annotation { "Feature Type Name" : "Feature", "Feature Type Description" : "" }
export const myFeature = defineFeature(function(context is Context, id is Id, definition is map)
    precondition{}
    {
        {
            var Q0;
            Q0=qCreatedBy(makeId("Front.planeOp"),FACE);
            var sketch = newSketch(context, id + "F0", { "sketchPlane" : qUnion([Q0])});
            skLineSegment(sketch, "E0.1", {"start": v(-0.04, 26) * mm, "end": v(22.5, 13.04) * mm});
            skLineSegment(sketch, "E0.2", {"start": v(22.5, 13.04) * mm, "end": v(22.54, -12.96) * mm});
            skLineSegment(sketch, "E0.3", {"start": v(22.54, -12.96) * mm, "end": v(15.83, -16.85) * mm});
            skLineSegment(sketch, "E0.4", {"start": v(-6.46, -22.26) * mm, "end": v(-7.97, -21.4) * mm});
            skPoint(sketch, "E0.0.midPoint", {"position": v(-11.3, 19.48) * mm});
            skLineSegment(sketch, "E1", {"start": v(-0.04, 26) * mm, "end": v(0.04, -26) * mm});
            skLineSegment(sketch, "E2.0", {"start": v(7.98, 13.23) * mm, "end": v(8.04, -21.37) * mm});
            skLineSegment(sketch, "E3.0", {"start": v(15.78, 9.24) * mm, "end": v(15.83, -16.85) * mm});
            skLineSegment(sketch, "E4", {"start": v(6.48, 14) * mm, "end": v(7.98, 13.23) * mm});
            skLineSegment(sketch, "E5.0", {"start": v(6.48, 14) * mm, "end": v(6.54, -22.24) * mm});
            skLineSegment(sketch, "E6.0", {"start": v(14.28, 10) * mm, "end": v(14.33, -17.72) * mm});
            skLineSegment(sketch, "E7.trimOffspring", {"start": v(14.28, 10) * mm, "end": v(15.78, 9.24) * mm});
            skLineSegment(sketch, "E8.trimOffspring", {"start": v(6.54, -22.24) * mm, "end": v(0.04, -26) * mm});
            skLineSegment(sketch, "E9.trimOffspring", {"start": v(14.33, -17.72) * mm, "end": v(8.04, -21.37) * mm});
            skLineSegment(sketch, "E10.MirrorCS", {"start": v(-8.02, 13.2) * mm, "end": v(-7.96, -21.4) * mm});
            skLineSegment(sketch, "E11.MirrorCS", {"start": v(-15.82, 9.18) * mm, "end": v(-15.77, -16.9) * mm});
            skLineSegment(sketch, "E12.0", {"start": v(-6.52, 13.23) * mm, "end": v(-6.47, -21.37) * mm});
            skLineSegment(sketch, "E13", {"start": v(-8.02, 14) * mm, "end": v(-6.52, 13.23) * mm});
            skLineSegment(sketch, "E14.0", {"start": v(-8.02, 14) * mm, "end": v(-7.97, -21.4) * mm});
            skLineSegment(sketch, "E15.0", {"start": v(-14.32, 9.19) * mm, "end": v(-14.27, -16.9) * mm});
            skLineSegment(sketch, "E16.0", {"start": v(-15.82, 9.96) * mm, "end": v(-15.77, -16.9) * mm});
            skLineSegment(sketch, "E17.trimOffspring", {"start": v(-15.82, 9.96) * mm, "end": v(-14.32, 9.19) * mm});
            skPoint(sketch, "E18.orphan", {"position": v(-14.32, 9.96) * mm});
            skPoint(sketch, "E19.MirrorCS.end.orphan", {"position": v(-14.27, -17.77) * mm});
            skPoint(sketch, "E20.MirrorCS.end.orphan", {"position": v(-15.82, 9.18) * mm});
            skPoint(sketch, "E21.orphan", {"position": v(-6.52, 13.98) * mm});
            skPoint(sketch, "E22.MirrorCS.end.orphan", {"position": v(-6.46, -22.26) * mm});
            skPoint(sketch, "E23.MirrorCS.end.orphan", {"position": v(-8.02, 13.2) * mm});
            skPoint(sketch, "E24.orphan", {"position": v(-15.77, -17.77) * mm});
            skPoint(sketch, "E25.orphan", {"position": v(-7.96, -22.24) * mm});
            skLineSegment(sketch, "E26", {"start": v(-14.27, -16.9) * mm, "end": v(-14.27, -17.77) * mm});
            skLineSegment(sketch, "E27", {"start": v(-6.47, -21.37) * mm, "end": v(-6.46, -22.26) * mm});
            skLineSegment(sketch, "E28.trimOffspring", {"start": v(-14.27, -17.77) * mm, "end": v(-15.77, -16.9) * mm});
            skPoint(sketch, "E29.orphan", {"position": v(-22.54, 12.96) * mm});
            skText(sketch, "E30", { "text": "MEISTER AUDIO", "fontName": "OpenSans-Regular.ttf"});
            const initialGuessF0  = {"E30": [0.031, -0.00792, 1, 0, 0.01685]};
            skSetInitialGuess(sketch, initialGuessF0);
            skSolve(sketch);
        }
        {
            var Q0;
            Q0=makeQuery(id+"F0.imprint","IMPRINT",FACE,{"disambiguationData":[TD([[makeQuery(id+"F0.imprint","IMPRINT",EDGE,{"derivedFrom":sQuery(id+"F0.wireOp",EDGE,"E15.0")}),-1.0]])]});
            var Q1;
            Q1=makeQuery(id+"F0.imprint","IMPRINT",FACE,{"disambiguationData":[TD([[makeQuery(id+"F0.imprint","IMPRINT",EDGE,{"derivedFrom":sQuery(id+"F0.wireOp",EDGE,"E12.0")}),-1.0]])]});
            var Q2;
            Q2=makeQuery(id+"F0.imprint","IMPRINT",FACE,{"disambiguationData":[TD([[makeQuery(id+"F0.imprint","IMPRINT",EDGE,{"derivedFrom":sQuery(id+"F0.wireOp",EDGE,"E0.1")}),-1.0]])]});
            extrude(context, id + "F1", {"entities" : qUnion([Q0, Q1, Q2]), "depth" : 3 * mm, "offsetDistance" : 25 * mm});
        }
        {
            var Q0;
            Q0 = qSketchRegion(id + "F0", true);
            extrude(context, id + "F2", {"entities" : qUnion([Q0]), "depth" : 3 * mm, "offsetDistance" : 25 * mm});
        }
    });